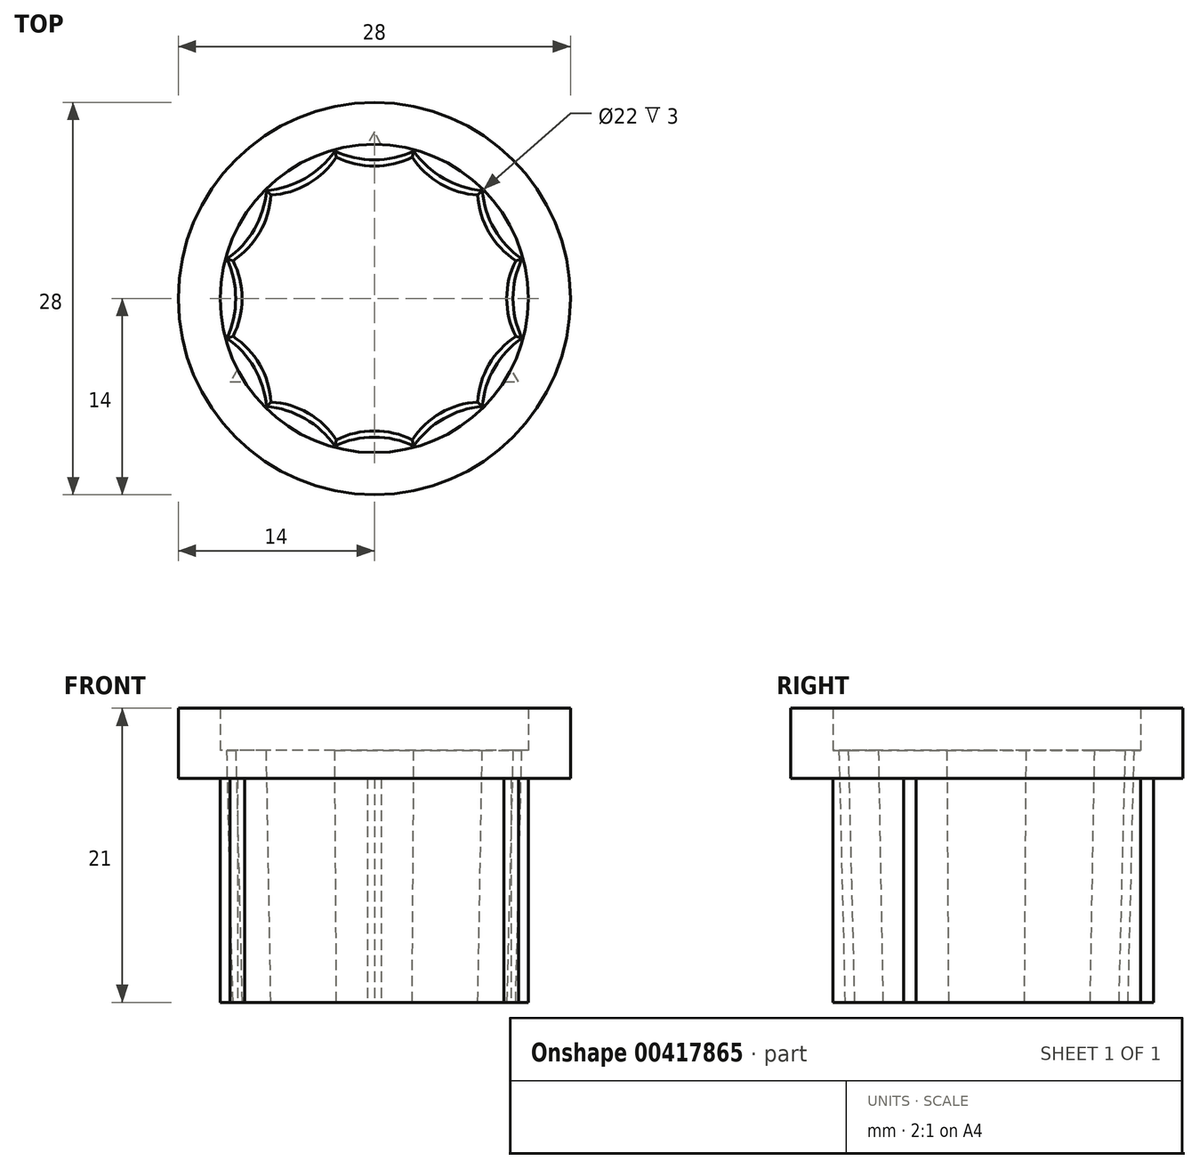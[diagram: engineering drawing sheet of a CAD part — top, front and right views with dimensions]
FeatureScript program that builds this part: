
annotation { "Feature Type Name" : "Feature", "Feature Type Description" : "" }
export const myFeature = defineFeature(function(context is Context, id is Id, definition is map)
    precondition{}
    {
        {
            var Q0;
            Q0=qCreatedBy(makeId("Top.planeOp"),FACE);
            var sketch = newSketch(context, id + "F0", { "sketchPlane" : qUnion([Q0])});
            skCircle(sketch, "E0", {"center": v(0, 0) * mm, "radius": 10.45 * mm, "construction": true});
            skCircle(sketch, "E1", {"center": v(0, 0) * mm, "radius": 9.45 * mm, "construction": true});
            skCircle(sketch, "E2", {"center": v(0, 0) * mm, "radius": 14 * mm});
            skLineSegment(sketch, "E3", {"start": v(0, 0) * mm, "end": v(-2.7, 10.1) * mm, "construction": true});
            skLineSegment(sketch, "E4", {"start": v(0, 0) * mm, "end": v(0, 0) * mm});
            skLineSegment(sketch, "E5", {"start": v(0, 0) * mm, "end": v(2.7, 10.1) * mm, "construction": true});
            skArc(sketch, "E6", {"start": v(-2.7, 10.1) * mm, "mid": v(0, 9.45) * mm, "end": v(2.7, 10.1) * mm});
            skArc(sketch, "E7.1.0", {"start": v(-7.39, 7.39) * mm, "mid": v(-4.72, 8.18) * mm, "end": v(-2.7, 10.1) * mm});
            skArc(sketch, "E7.2.0", {"start": v(-10.1, 2.7) * mm, "mid": v(-8.18, 4.73) * mm, "end": v(-7.39, 7.39) * mm});
            skArc(sketch, "E8.2.3.0", {"start": v(-10.1, -2.7) * mm, "mid": v(-9.45, 0) * mm, "end": v(-10.1, 2.7) * mm});
            skArc(sketch, "E8.2.4.0", {"start": v(-7.39, -7.39) * mm, "mid": v(-8.18, -4.72) * mm, "end": v(-10.1, -2.7) * mm});
            skArc(sketch, "E8.2.5.0", {"start": v(-2.7, -10.1) * mm, "mid": v(-4.73, -8.18) * mm, "end": v(-7.39, -7.39) * mm});
            skArc(sketch, "E8.2.6.0", {"start": v(2.7, -10.1) * mm, "mid": v(0, -9.45) * mm, "end": v(-2.7, -10.1) * mm});
            skArc(sketch, "E8.2.7.0", {"start": v(7.39, -7.39) * mm, "mid": v(4.72, -8.18) * mm, "end": v(2.7, -10.1) * mm});
            skArc(sketch, "E8.2.8.0", {"start": v(10.1, -2.7) * mm, "mid": v(8.18, -4.73) * mm, "end": v(7.39, -7.39) * mm});
            skArc(sketch, "E8.2.9.0", {"start": v(10.1, 2.7) * mm, "mid": v(9.45, 0) * mm, "end": v(10.1, -2.7) * mm});
            skArc(sketch, "E8.2.10.0", {"start": v(7.39, 7.39) * mm, "mid": v(8.18, 4.72) * mm, "end": v(10.1, 2.7) * mm});
            skArc(sketch, "E8.2.11.0", {"start": v(2.7, 10.1) * mm, "mid": v(4.72, 8.18) * mm, "end": v(7.39, 7.39) * mm});
            skCircle(sketch, "E9", {"center": v(0, 0) * mm, "radius": 15.45 * mm, "construction": true});
            skSolve(sketch);
        }
        {
            var Q0;
            Q0=qCreatedBy(makeId("Top.planeOp"),FACE);
            cPlane(context, id + "F1", {"entities" : qUnion([Q0]), "cplaneType" : CPlaneType.OFFSET, "offset" : 18 * mm, "width" : 150 * mm, "height" : 150 * mm});
        }
        {
            var Q0;
            Q0=qCreatedBy(id+"F1.planeOp",FACE);
            var sketch = newSketch(context, id + "F2", { "sketchPlane" : qUnion([Q0])});
            skCircle(sketch, "E10", {"center": v(0, 0) * mm, "radius": 10.9 * mm, "construction": true});
            skCircle(sketch, "E11", {"center": v(0, 0) * mm, "radius": 9.9 * mm, "construction": true});
            skLineSegment(sketch, "E12", {"start": v(0, 0) * mm, "end": v(-2.82, 10.53) * mm, "construction": true});
            skLineSegment(sketch, "E13", {"start": v(0, 0) * mm, "end": v(2.82, 10.53) * mm, "construction": true});
            skArc(sketch, "E14", {"start": v(-2.82, 10.53) * mm, "mid": v(0, 9.9) * mm, "end": v(2.82, 10.53) * mm});
            skArc(sketch, "E15.1.0", {"start": v(-7.7, 7.7) * mm, "mid": v(-4.95, 8.57) * mm, "end": v(-2.82, 10.53) * mm});
            skArc(sketch, "E15.2.0", {"start": v(-10.53, 2.82) * mm, "mid": v(-8.57, 4.95) * mm, "end": v(-7.7, 7.7) * mm});
            skArc(sketch, "E16.2.3.0", {"start": v(-10.53, -2.82) * mm, "mid": v(-9.9, 0) * mm, "end": v(-10.53, 2.82) * mm});
            skArc(sketch, "E16.2.4.0", {"start": v(-7.7, -7.7) * mm, "mid": v(-8.57, -4.95) * mm, "end": v(-10.53, -2.82) * mm});
            skArc(sketch, "E16.2.5.0", {"start": v(-2.82, -10.53) * mm, "mid": v(-4.95, -8.57) * mm, "end": v(-7.7, -7.7) * mm});
            skArc(sketch, "E16.2.6.0", {"start": v(2.82, -10.53) * mm, "mid": v(0, -9.9) * mm, "end": v(-2.82, -10.53) * mm});
            skArc(sketch, "E16.2.7.0", {"start": v(7.7, -7.7) * mm, "mid": v(4.95, -8.57) * mm, "end": v(2.82, -10.53) * mm});
            skArc(sketch, "E16.2.8.0", {"start": v(10.53, -2.82) * mm, "mid": v(8.57, -4.95) * mm, "end": v(7.7, -7.7) * mm});
            skArc(sketch, "E16.2.9.0", {"start": v(10.53, 2.82) * mm, "mid": v(9.9, 0) * mm, "end": v(10.53, -2.82) * mm});
            skArc(sketch, "E16.2.10.0", {"start": v(7.7, 7.7) * mm, "mid": v(8.57, 4.95) * mm, "end": v(10.53, 2.82) * mm});
            skArc(sketch, "E16.2.11.0", {"start": v(2.82, 10.53) * mm, "mid": v(4.95, 8.57) * mm, "end": v(7.7, 7.7) * mm});
            skCircle(sketch, "E17", {"center": v(0, 0) * mm, "radius": 11 * mm});
            skCircle(sketch, "E18", {"center": v(0, 0) * mm, "radius": 14 * mm});
            skCircle(sketch, "E19", {"center": v(0, 0) * mm, "radius": 16.54 * mm, "construction": true});
            skSolve(sketch);
        }
        {
            var Q0;
            Q0=makeQuery(id+"F0.imprint","IMPRINT",FACE,{"disambiguationData":[TD([[makeQuery(id+"F0.imprint","IMPRINT",EDGE,{"derivedFrom":sQuery(id+"F0.wireOp",EDGE,"E2")}),1.0]])]});
            var Q1;
            Q1=makeQuery(id+"F0.imprint","IMPRINT",FACE,{"disambiguationData":[TD([[makeQuery(id+"F0.imprint","IMPRINT",EDGE,{"derivedFrom":sQuery(id+"F0.wireOp",EDGE,"E6")}),-1.0]])]});
            var Q2;
            Q2=qCreatedBy(id+"F1.planeOp",FACE);
            extrude(context, id + "F3", {"entities" : qUnion([Q0, Q1]), "endBound" : BoundingType.UP_TO_SURFACE, "depth" : 25 * mm, "endBoundEntityFace" : qUnion([Q2]), "offsetDistance" : 25 * mm});
        }
        {
            var Q1;
            Q1=makeQuery(id+"F0.imprint","IMPRINT",FACE,{"disambiguationData":[TD([[makeQuery(id+"F0.imprint","IMPRINT",EDGE,{"derivedFrom":sQuery(id+"F0.wireOp",EDGE,"E6")}),-1.0]])]});
            var Q2;
            Q2=makeQuery(id+"F2.imprint","IMPRINT",FACE,{"disambiguationData":[TD([[makeQuery(id+"F2.imprint","IMPRINT",EDGE,{"derivedFrom":sQuery(id+"F2.wireOp",EDGE,"E14")}),-1.0]])]});
            loft(context, id + "F4", {"operationType" : NewBodyOperationType.REMOVE, "sheetProfilesArray" : [{ "sheetProfileEntities" : qUnion([Q1]) }, { "sheetProfileEntities" : qUnion([Q2]) }]});
        }
        {
            var Q0;
            Q0=makeQuery(id+"F2.imprint","IMPRINT",FACE,{"disambiguationData":[TD([[makeQuery(id+"F2.imprint","IMPRINT",EDGE,{"derivedFrom":sQuery(id+"F2.wireOp",EDGE,"E17")}),-1.0]])]});
            extrude(context, id + "F5", {"entities" : qUnion([Q0]), "operationType" : NewBodyOperationType.ADD, "depth" : 3 * mm, "offsetDistance" : 25 * mm});
        }
        {
            var Q0;
            Q0=qCreatedBy(makeId("Top.planeOp"),FACE);
            var sketch = newSketch(context, id + "F6", { "sketchPlane" : qUnion([Q0])});
            skArc(sketch, "E20", {"start": v(-0.5, 10.99) * mm, "mid": v(-9.53, 5.5) * mm, "end": v(-9.77, -5.06) * mm});
            skLineSegment(sketch, "E21", {"start": v(0.5, 10.99) * mm, "end": v(0, 11.9) * mm});
            skLineSegment(sketch, "E22", {"start": v(0, 11.9) * mm, "end": v(-0.5, 10.99) * mm});
            skLineSegment(sketch, "E23.1.0", {"start": v(-9.77, -5.06) * mm, "end": v(-10.3, -5.95) * mm});
            skLineSegment(sketch, "E23.1.1", {"start": v(-10.3, -5.95) * mm, "end": v(-9.27, -5.93) * mm});
            skLineSegment(sketch, "E23.2.0", {"start": v(9.27, -5.93) * mm, "end": v(10.3, -5.95) * mm});
            skLineSegment(sketch, "E23.2.1", {"start": v(10.3, -5.95) * mm, "end": v(9.77, -5.06) * mm});
            skArc(sketch, "E24.trimOffspring", {"start": v(-9.27, -5.93) * mm, "mid": v(0, -11) * mm, "end": v(9.27, -5.93) * mm});
            skArc(sketch, "E25.trimOffspring", {"start": v(9.77, -5.06) * mm, "mid": v(9.53, 5.5) * mm, "end": v(0.5, 10.99) * mm});
            skCircle(sketch, "E26", {"center": v(0, 0) * mm, "radius": 14 * mm});
            skSolve(sketch);
        }
        {
            var Q0;
            Q0=makeQuery(id+"F6.imprint","IMPRINT",FACE,{"disambiguationData":[TD([[makeQuery(id+"F6.imprint","IMPRINT",EDGE,{"derivedFrom":sQuery(id+"F6.wireOp",EDGE,"E20")}),-1.0]])]});
            extrude(context, id + "F7", {"entities" : qUnion([Q0]), "operationType" : NewBodyOperationType.REMOVE, "depth" : 16 * mm, "offsetDistance" : 25 * mm});
        }
    });
